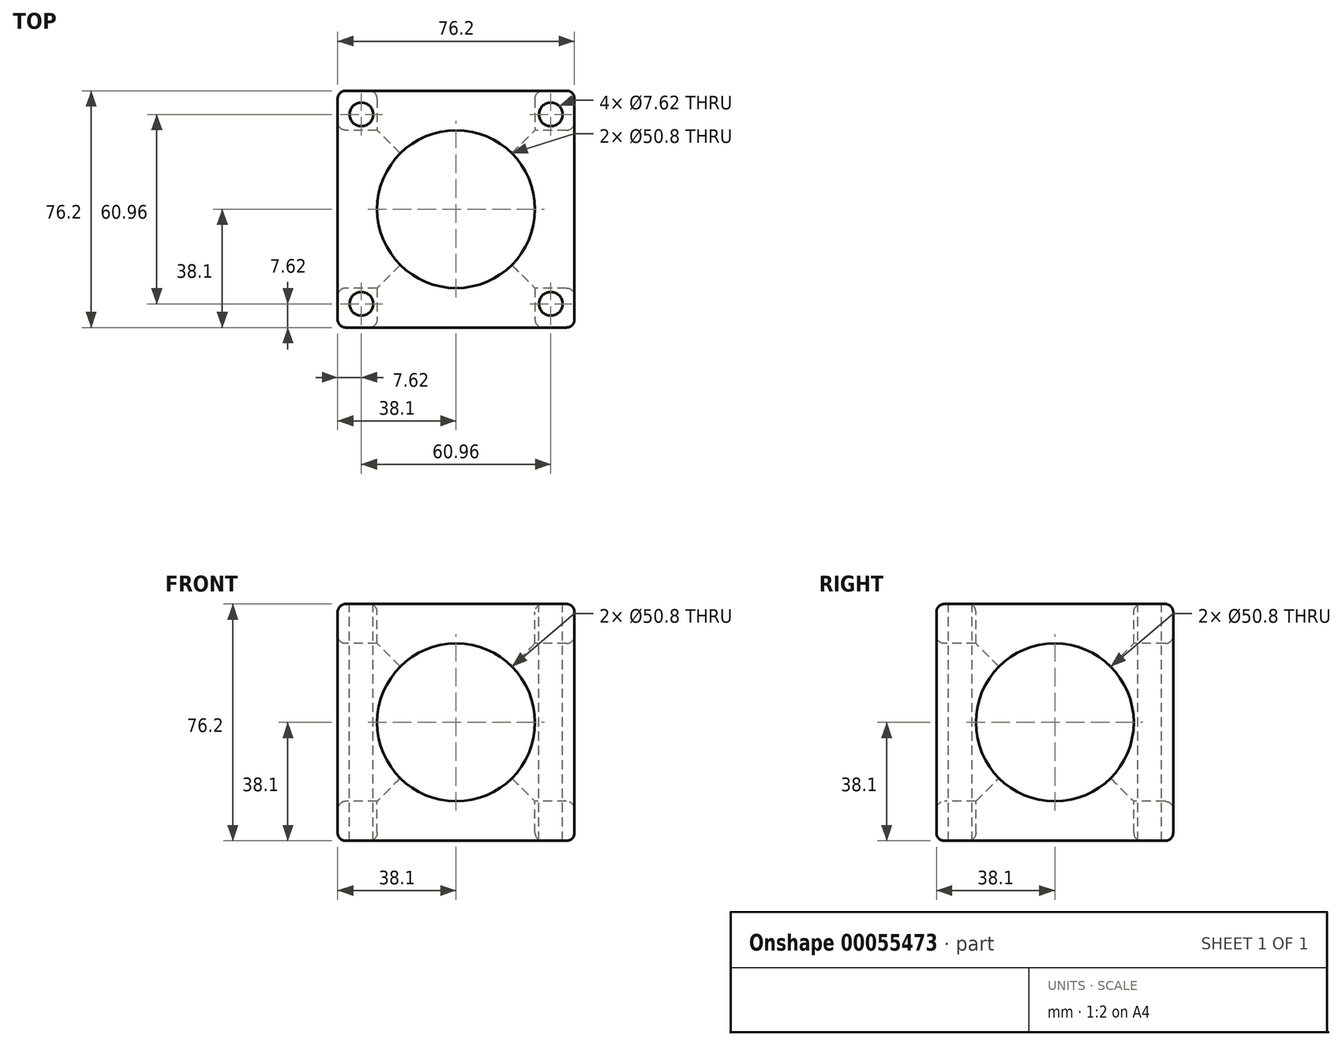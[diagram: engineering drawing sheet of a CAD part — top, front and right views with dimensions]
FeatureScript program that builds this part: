
annotation { "Feature Type Name" : "Feature", "Feature Type Description" : "" }
export const myFeature = defineFeature(function(context is Context, id is Id, definition is map)
    precondition{}
    {
        {
            var Q0;
            Q0=qCreatedBy(makeId("Front.planeOp"),FACE);
            var sketch = newSketch(context, id + "F0", { "sketchPlane" : qUnion([Q0])});
            skLineSegment(sketch, "E0.bottom", {"start": v(0, 0) * mm, "end": v(76.2, 0) * mm});
            skLineSegment(sketch, "E0.top", {"start": v(0, -76.2) * mm, "end": v(76.2, -76.2) * mm});
            skLineSegment(sketch, "E0.left", {"start": v(0, 0) * mm, "end": v(0, -76.2) * mm});
            skLineSegment(sketch, "E0.right", {"start": v(76.2, 0) * mm, "end": v(76.2, -76.2) * mm});
            skSolve(sketch);
        }
        {
            var Q0;
            Q0=makeQuery(id+"F0.imprint","IMPRINT",FACE,{"disambiguationData":[TD([[makeQuery(id+"F0.imprint","IMPRINT",EDGE,{"derivedFrom":sQuery(id+"F0.wireOp",EDGE,"E0.bottom")}),-1.0]])]});
            extrude(context, id + "F1", {"entities" : qUnion([Q0]), "depth" : 76.2 * mm});
        }
        {
            var Q0;
            Q0=makeQuery(id+"F1.opExtrude","CAP_FACE",FACE,{"disambiguationData":[OSD([sQuery(id+"F0.wireOp",EDGE,"E0.bottom"),sQuery(id+"F0.wireOp",EDGE,"E0.top"),sQuery(id+"F0.wireOp",EDGE,"E0.left"),sQuery(id+"F0.wireOp",EDGE,"E0.right")])],"isStart":false});
            var sketch = newSketch(context, id + "F2", { "sketchPlane" : qUnion([Q0])});
            skCircle(sketch, "E1", {"center": v(38.1, -38.1) * mm, "radius": 25.4 * mm});
            skSolve(sketch);
        }
        {
            var Q0;
            Q0=makeQuery(id+"F2.imprint","IMPRINT",FACE,{"disambiguationData":[TD([[makeQuery(id+"F2.imprint","IMPRINT",EDGE,{"derivedFrom":sQuery(id+"F2.wireOp",EDGE,"E1")}),1.0]])]});
            extrude(context, id + "F3", {"entities" : qUnion([Q0]), "operationType" : NewBodyOperationType.REMOVE, "endBound" : BoundingType.THROUGH_ALL, "oppositeDirection" : true, "depth" : 25.4 * mm});
        }
        {
            var Q0;
            Q0=makeQuery(id+"F1.opExtrude","SWEPT_FACE",FACE,{"disambiguationData":[OSD([sQuery(id+"F0.wireOp",EDGE,"E0.bottom")])]});
            var sketch = newSketch(context, id + "F4", { "sketchPlane" : qUnion([Q0])});
            skLineSegment(sketch, "E2", {"start": v(0, 0) * mm, "end": v(76.2, -76.2) * mm});
            skCircle(sketch, "E3", {"center": v(38.1, -38.1) * mm, "radius": 25.4 * mm});
            skSolve(sketch);
        }
        {
            var Q0;
            Q0 = qSketchRegion(id + "F4", true);
            extrude(context, id + "F5", {"entities" : qUnion([Q0]), "operationType" : NewBodyOperationType.REMOVE, "endBound" : BoundingType.THROUGH_ALL, "oppositeDirection" : true, "depth" : 25.4 * mm});
        }
        {
            var Q0;
            Q0=makeQuery(id+"F1.opExtrude","SWEPT_FACE",FACE,{"disambiguationData":[OSD([sQuery(id+"F0.wireOp",EDGE,"E0.left")])]});
            var sketch = newSketch(context, id + "F6", { "sketchPlane" : qUnion([Q0])});
            skLineSegment(sketch, "E4", {"start": v(0, 0) * mm, "end": v(76.2, -76.2) * mm});
            skCircle(sketch, "E5", {"center": v(38.1, -38.1) * mm, "radius": 25.4 * mm});
            skSolve(sketch);
        }
        {
            var Q0;
            Q0 = qSketchRegion(id + "F6", true);
            extrude(context, id + "F7", {"entities" : qUnion([Q0]), "operationType" : NewBodyOperationType.REMOVE, "endBound" : BoundingType.THROUGH_ALL, "oppositeDirection" : true, "depth" : 25.4 * mm});
        }
        {
            var Q0;
            Q0=makeQuery(id+"F1.opExtrude","SWEPT_FACE",FACE,{"disambiguationData":[OSD([sQuery(id+"F0.wireOp",EDGE,"E0.bottom")])]});
            var Q1;
            Q1=makeQuery(id+"F1.opExtrude","SWEPT_FACE",FACE,{"disambiguationData":[OSD([sQuery(id+"F0.wireOp",EDGE,"E0.right")])]});
            var Q2;
            Q2=makeQuery(id+"F1.opExtrude","CAP_FACE",FACE,{"disambiguationData":[OSD([sQuery(id+"F0.wireOp",EDGE,"E0.bottom"),sQuery(id+"F0.wireOp",EDGE,"E0.top"),sQuery(id+"F0.wireOp",EDGE,"E0.left"),sQuery(id+"F0.wireOp",EDGE,"E0.right")])],"isStart":false});
            var Q3;
            Q3=makeQuery(id+"F1.opExtrude","SWEPT_FACE",FACE,{"disambiguationData":[OSD([sQuery(id+"F0.wireOp",EDGE,"E0.top")])]});
            var Q4;
            Q4=makeQuery(id+"F1.opExtrude","CAP_EDGE",EDGE,{"disambiguationData":[OSD([sQuery(id+"F0.wireOp",EDGE,"E0.top")])],"isStart":true});
            var Q5;
            Q5=makeQuery(id+"F1.opExtrude","SWEPT_FACE",FACE,{"disambiguationData":[OSD([sQuery(id+"F0.wireOp",EDGE,"E0.left")])]});
            var Q6;
            Q6=makeQuery(id+"F1.opExtrude","CAP_FACE",FACE,{"disambiguationData":[OSD([sQuery(id+"F0.wireOp",EDGE,"E0.bottom"),sQuery(id+"F0.wireOp",EDGE,"E0.top"),sQuery(id+"F0.wireOp",EDGE,"E0.left"),sQuery(id+"F0.wireOp",EDGE,"E0.right")])],"isStart":true});
            fillet(context, id + "F8", {"entities" : qUnion([Q0, Q1, Q2, Q3, Q4, Q5, Q6]), "radius" : 2.54 * mm, "tangentPropagation" : true, "allowEdgeOverflow" : false});
        }
        {
            var Q0;
            Q0=makeQuery(id+"F1.opExtrude","SWEPT_FACE",FACE,{"disambiguationData":[OSD([sQuery(id+"F0.wireOp",EDGE,"E0.bottom")])]});
            var sketch = newSketch(context, id + "F9", { "sketchPlane" : qUnion([Q0])});
            skCircle(sketch, "E6", {"center": v(68.58, -7.62) * mm, "radius": 3.81 * mm});
            skCircle(sketch, "E7", {"center": v(68.58, -68.58) * mm, "radius": 3.81 * mm});
            skCircle(sketch, "E8", {"center": v(7.62, -68.58) * mm, "radius": 3.81 * mm});
            skCircle(sketch, "E9", {"center": v(7.62, -7.62) * mm, "radius": 3.81 * mm});
            skSolve(sketch);
        }
        {
            var Q0;
            Q0 = qSketchRegion(id + "F9", true);
            extrude(context, id + "F10", {"entities" : qUnion([Q0]), "operationType" : NewBodyOperationType.REMOVE, "endBound" : BoundingType.THROUGH_ALL, "oppositeDirection" : true, "depth" : 12.7 * mm});
        }
    });
